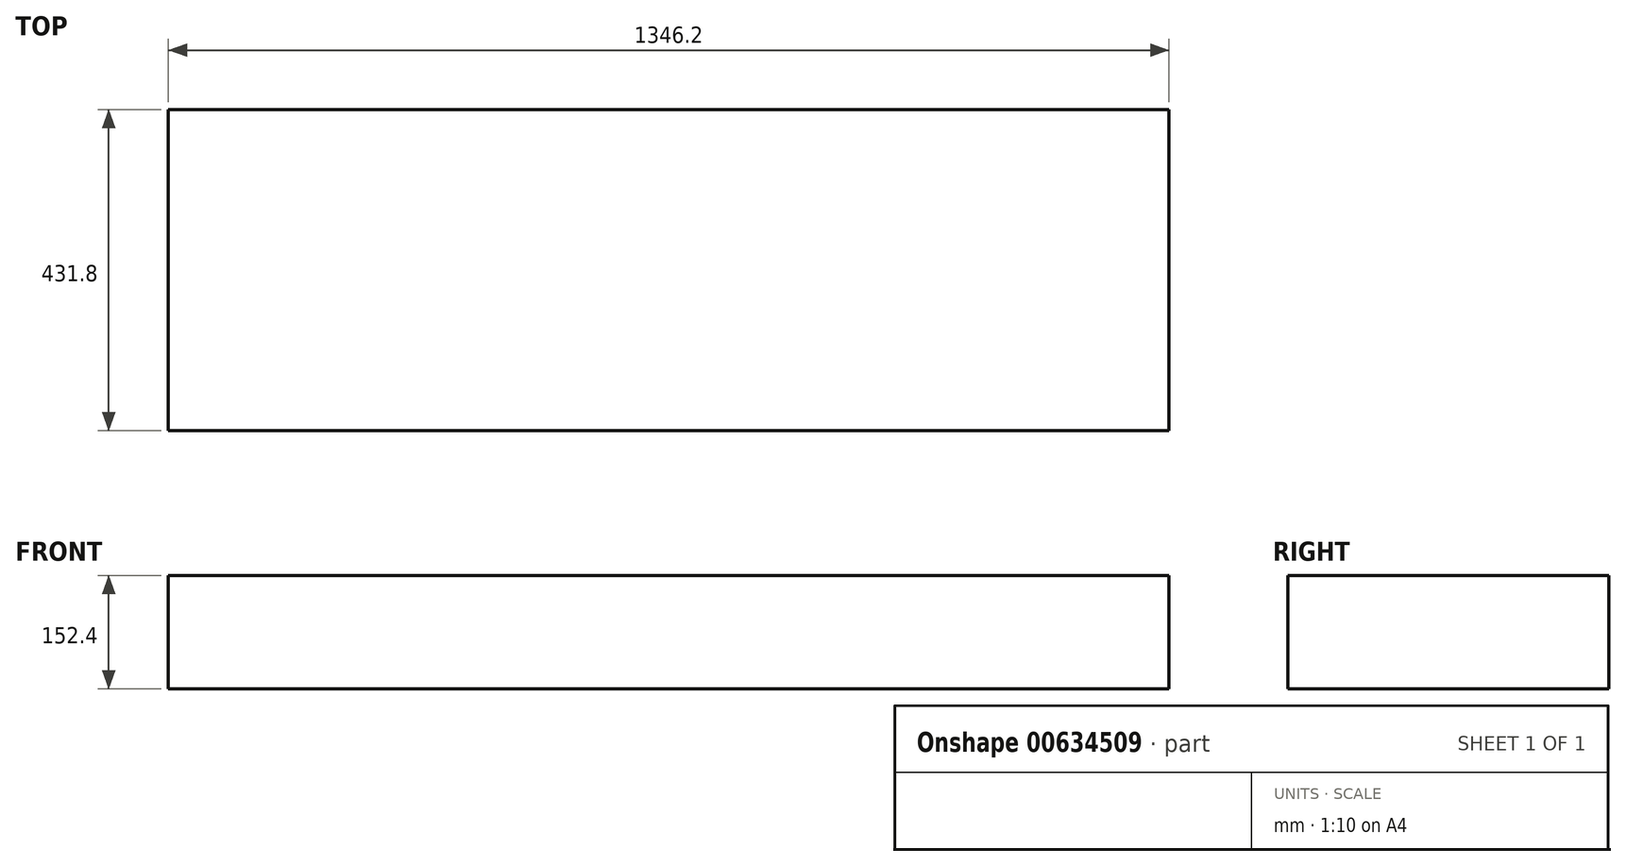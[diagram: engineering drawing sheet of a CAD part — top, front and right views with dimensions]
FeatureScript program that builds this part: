
annotation { "Feature Type Name" : "Feature", "Feature Type Description" : "" }
export const myFeature = defineFeature(function(context is Context, id is Id, definition is map)
    precondition{}
    {
        {
            var Q0;
            Q0=qCreatedBy(makeId("Top.planeOp"),FACE);
            var sketch = newSketch(context, id + "F0", { "sketchPlane" : qUnion([Q0])});
            skLineSegment(sketch, "E0.bottom", {"start": v(0, 0) * mm, "end": v(1346.2, 0) * mm});
            skLineSegment(sketch, "E0.top", {"start": v(0, 431.8) * mm, "end": v(1346.2, 431.8) * mm});
            skLineSegment(sketch, "E0.left", {"start": v(0, 0) * mm, "end": v(0, 431.8) * mm});
            skLineSegment(sketch, "E0.right", {"start": v(1346.2, 0) * mm, "end": v(1346.2, 431.8) * mm});
            skSolve(sketch);
        }
        {
            var Q0;
            Q0=makeQuery(id+"F0.imprint","IMPRINT",FACE,{"disambiguationData":[TD([[makeQuery(id+"F0.imprint","IMPRINT",EDGE,{"derivedFrom":sQuery(id+"F0.wireOp",EDGE,"E0.bottom")}),1.0]])]});
            extrude(context, id + "F1", {"entities" : qUnion([Q0]), "depth" : 152.4 * mm});
        }
    });
